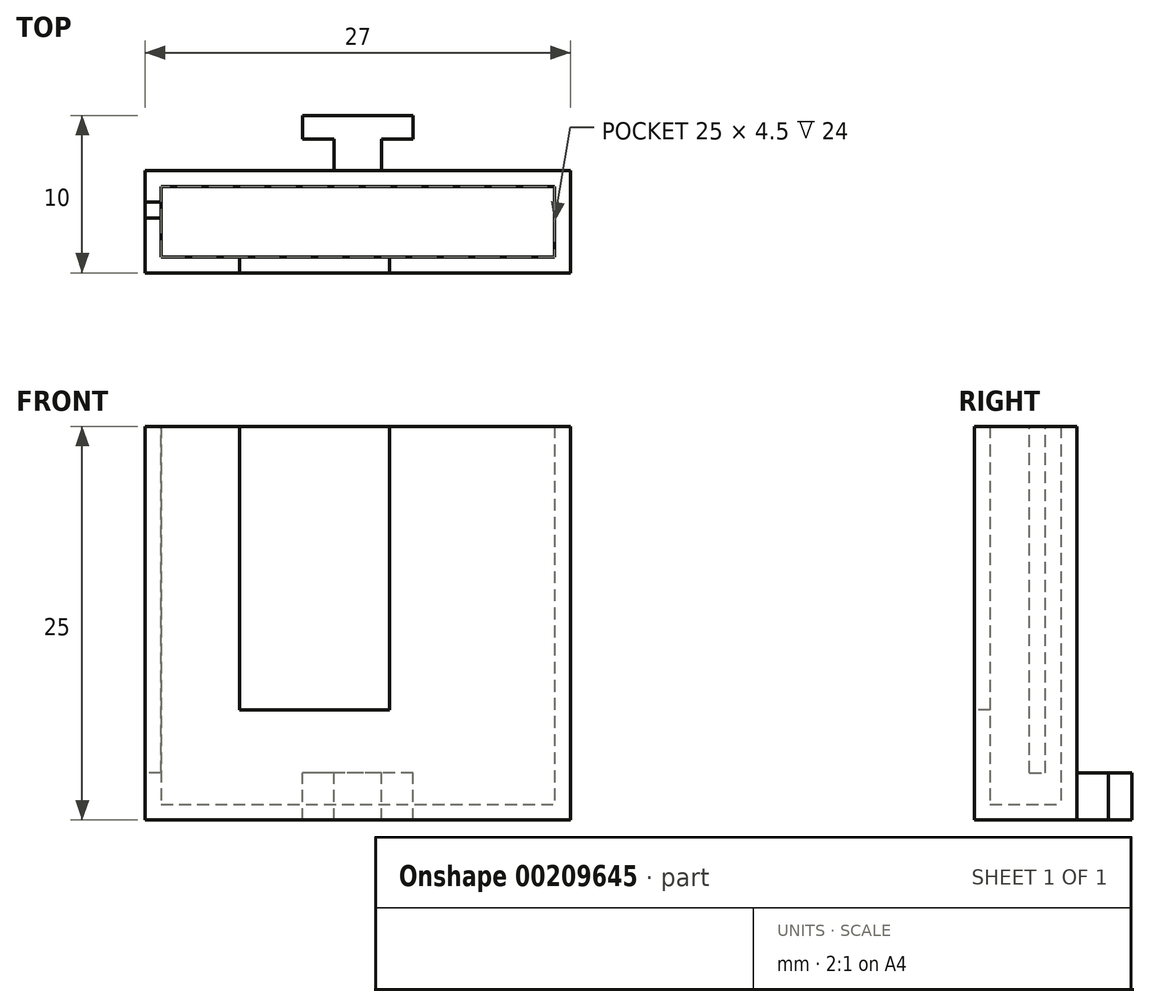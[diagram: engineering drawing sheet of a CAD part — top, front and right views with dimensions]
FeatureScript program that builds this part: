
annotation { "Feature Type Name" : "Feature", "Feature Type Description" : "" }
export const myFeature = defineFeature(function(context is Context, id is Id, definition is map)
    precondition{}
    {
        {
            var Q0;
            Q0=qCreatedBy(makeId("Top.planeOp"),FACE);
            var sketch = newSketch(context, id + "F0", { "sketchPlane" : qUnion([Q0])});
            skLineSegment(sketch, "E0.bottom", {"start": v(0, 0) * mm, "end": v(27, 0) * mm});
            skLineSegment(sketch, "E0.top", {"start": v(0, 6.5) * mm, "end": v(27, 6.5) * mm});
            skLineSegment(sketch, "E0.left", {"start": v(0, 0) * mm, "end": v(0, 6.5) * mm});
            skLineSegment(sketch, "E0.right", {"start": v(27, 0) * mm, "end": v(27, 6.5) * mm});
            skSolve(sketch);
        }
        {
            var Q0;
            Q0=makeQuery(id+"F0.imprint","IMPRINT",FACE,{"disambiguationData":[TD([[makeQuery(id+"F0.imprint","IMPRINT",EDGE,{"derivedFrom":sQuery(id+"F0.wireOp",EDGE,"E0.bottom")}),1.0]])]});
            extrude(context, id + "F1", {"entities" : qUnion([Q0]), "depth" : 25 * mm});
        }
        {
            var Q0;
            Q0=makeQuery(id+"F1.opExtrude","CAP_FACE",FACE,{"disambiguationData":[OSD([sQuery(id+"F0.wireOp",EDGE,"E0.bottom"),sQuery(id+"F0.wireOp",EDGE,"E0.top"),sQuery(id+"F0.wireOp",EDGE,"E0.left"),sQuery(id+"F0.wireOp",EDGE,"E0.right")])],"isStart":false});
            shell(context, id + "F2", {"entities" : qUnion([Q0]), "thickness" : 1 * mm});
        }
        {
            var Q0;
            Q0=makeQuery(id+"F1.opExtrude","SWEPT_FACE",FACE,{"disambiguationData":[OSD([sQuery(id+"F0.wireOp",EDGE,"E0.bottom")])]});
            var sketch = newSketch(context, id + "F3", { "sketchPlane" : qUnion([Q0])});
            skLineSegment(sketch, "E1.bottom", {"start": v(6, 25) * mm, "end": v(15.5, 25) * mm});
            skLineSegment(sketch, "E1.top", {"start": v(6, 7) * mm, "end": v(15.5, 7) * mm});
            skLineSegment(sketch, "E1.left", {"start": v(6, 25) * mm, "end": v(6, 7) * mm});
            skLineSegment(sketch, "E1.right", {"start": v(15.5, 25) * mm, "end": v(15.5, 7) * mm});
            skSolve(sketch);
        }
        {
            var Q0;
            Q0=makeQuery(id+"F3.imprint","IMPRINT",FACE,{"disambiguationData":[TD([[makeQuery(id+"F3.imprint","IMPRINT",EDGE,{"derivedFrom":sQuery(id+"F3.wireOp",EDGE,"E1.bottom")}),-1.0]])]});
            extrude(context, id + "F4", {"entities" : qUnion([Q0]), "operationType" : NewBodyOperationType.REMOVE, "endBound" : BoundingType.UP_TO_NEXT, "oppositeDirection" : true, "depth" : 25 * mm});
        }
        {
            var Q0;
            Q0=makeQuery(id+"F1.opExtrude","SWEPT_FACE",FACE,{"disambiguationData":[OSD([sQuery(id+"F0.wireOp",EDGE,"E0.left")])]});
            var sketch = newSketch(context, id + "F5", { "sketchPlane" : qUnion([Q0])});
            skLineSegment(sketch, "E2.bottom", {"start": v(-4.5, 25) * mm, "end": v(-3.5, 25) * mm});
            skLineSegment(sketch, "E2.top", {"start": v(-4.5, 3) * mm, "end": v(-3.5, 3) * mm});
            skLineSegment(sketch, "E2.left", {"start": v(-4.5, 25) * mm, "end": v(-4.5, 3) * mm});
            skLineSegment(sketch, "E2.right", {"start": v(-3.5, 25) * mm, "end": v(-3.5, 3) * mm});
            skSolve(sketch);
        }
        {
            var Q0;
            Q0=makeQuery(id+"F5.imprint","IMPRINT",FACE,{"disambiguationData":[TD([[makeQuery(id+"F5.imprint","IMPRINT",EDGE,{"derivedFrom":sQuery(id+"F5.wireOp",EDGE,"E2.bottom")}),1.0]])]});
            extrude(context, id + "F6", {"entities" : qUnion([Q0]), "operationType" : NewBodyOperationType.REMOVE, "endBound" : BoundingType.UP_TO_NEXT, "oppositeDirection" : true, "depth" : 25 * mm});
        }
        {
            var Q0;
            Q0=makeQuery(id+"F1.opExtrude","SWEPT_FACE",FACE,{"disambiguationData":[OSD([sQuery(id+"F0.wireOp",EDGE,"E0.top")])]});
            var sketch = newSketch(context, id + "F7", { "sketchPlane" : qUnion([Q0])});
            skLineSegment(sketch, "E3.bottom", {"start": v(-15, 0) * mm, "end": v(-12, 0) * mm});
            skLineSegment(sketch, "E3.top", {"start": v(-15, 3) * mm, "end": v(-12, 3) * mm});
            skLineSegment(sketch, "E3.left", {"start": v(-15, 0) * mm, "end": v(-15, 3) * mm});
            skLineSegment(sketch, "E3.right", {"start": v(-12, 0) * mm, "end": v(-12, 3) * mm});
            skSolve(sketch);
        }
        {
            var Q0;
            Q0=makeQuery(id+"F7.imprint","IMPRINT",FACE,{"disambiguationData":[TD([[makeQuery(id+"F7.imprint","IMPRINT",EDGE,{"derivedFrom":sQuery(id+"F7.wireOp",EDGE,"E3.bottom")}),-1.0]])]});
            extrude(context, id + "F8", {"entities" : qUnion([Q0]), "operationType" : NewBodyOperationType.ADD, "depth" : 2 * mm});
        }
        {
            var Q0;
            Q0=makeQuery(id+"F8.opExtrude","CAP_FACE",FACE,{"disambiguationData":[OSD([sQuery(id+"F7.wireOp",EDGE,"E3.bottom"),sQuery(id+"F7.wireOp",EDGE,"E3.top"),sQuery(id+"F7.wireOp",EDGE,"E3.left"),sQuery(id+"F7.wireOp",EDGE,"E3.right")])],"isStart":false});
            var sketch = newSketch(context, id + "F9", { "sketchPlane" : qUnion([Q0])});
            skLineSegment(sketch, "E4.bottom", {"start": v(-17, 0) * mm, "end": v(-10, 0) * mm});
            skLineSegment(sketch, "E4.top", {"start": v(-17, 3) * mm, "end": v(-10, 3) * mm});
            skLineSegment(sketch, "E4.left", {"start": v(-17, 0) * mm, "end": v(-17, 3) * mm});
            skLineSegment(sketch, "E4.right", {"start": v(-10, 0) * mm, "end": v(-10, 3) * mm});
            skSolve(sketch);
        }
        {
            var Q0;
            {var subQ2=sQuery(id+"F9.wireOp",EDGE,"E4.right");Q0=makeQuery(id+"F9.imprint","IMPRINT",FACE,{"disambiguationData":[TD([[makeQuery(id+"F9.imprint","IMPRINT",EDGE,{"derivedFrom":subQ2}),1.0]])]});}
            var Q1;
            {var subQ2=makeQuery(id+"F8.opExtrude","CAP_EDGE",EDGE,{"disambiguationData":[OSD([sQuery(id+"F7.wireOp",EDGE,"E3.left")])],"isStart":false});Q1=makeQuery(id+"F9.imprint","IMPRINT",FACE,{"disambiguationData":[TD([[makeQuery(id+"F9.imprint","IMPRINT",EDGE,{"derivedFrom":subQ2}),-1.0]])]});}
            var Q2;
            {var subQ2=sQuery(id+"F9.wireOp",EDGE,"E4.left");Q2=makeQuery(id+"F9.imprint","IMPRINT",FACE,{"disambiguationData":[TD([[makeQuery(id+"F9.imprint","IMPRINT",EDGE,{"derivedFrom":subQ2}),-1.0]])]});}
            extrude(context, id + "F10", {"entities" : qUnion([Q0, Q1, Q2]), "operationType" : NewBodyOperationType.ADD, "depth" : 1.5 * mm});
        }
    });
